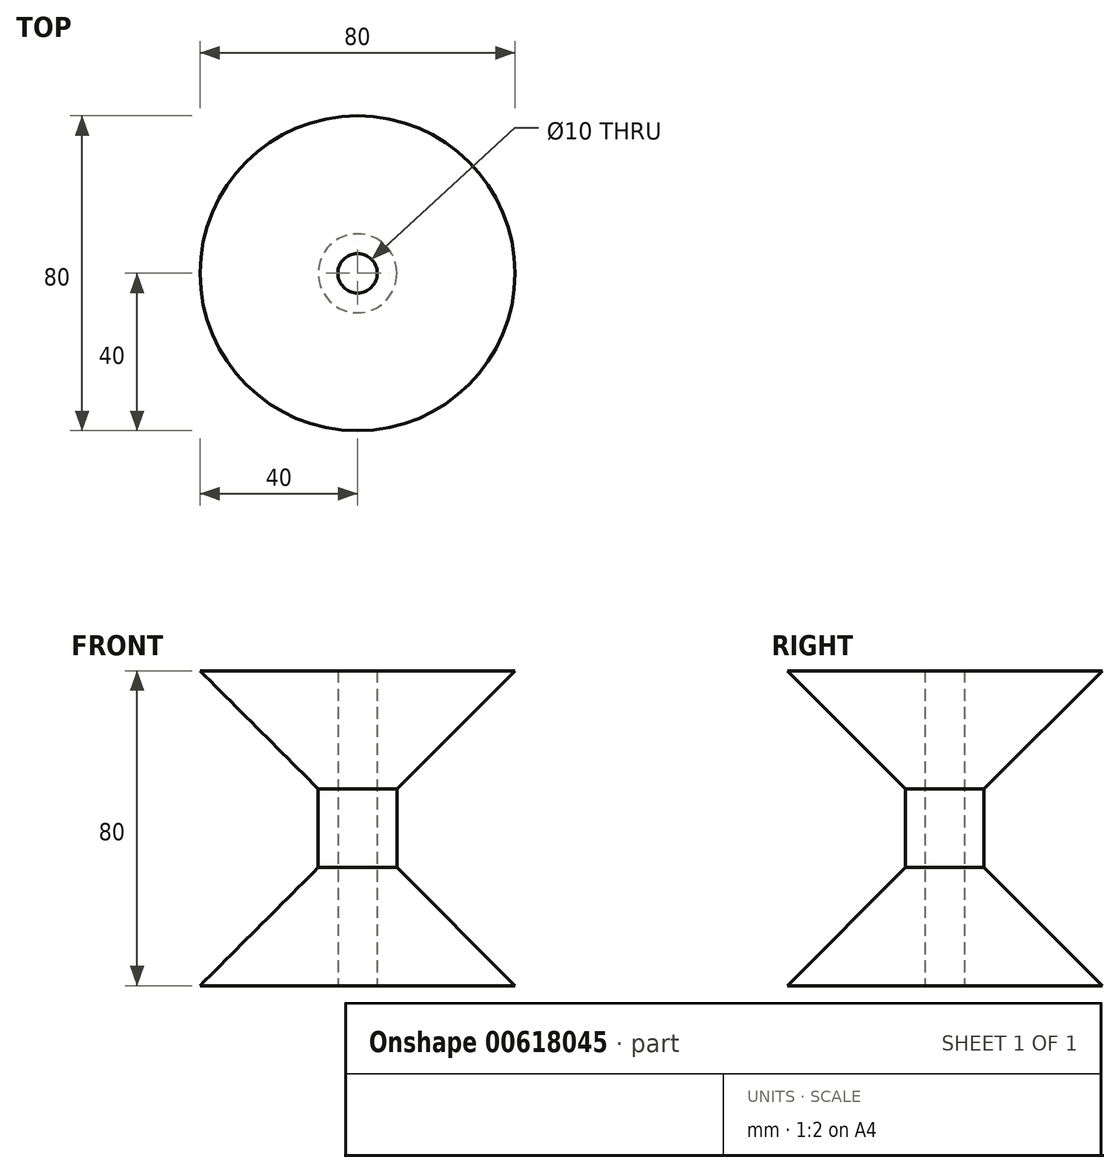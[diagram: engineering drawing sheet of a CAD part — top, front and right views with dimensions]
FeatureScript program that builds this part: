
annotation { "Feature Type Name" : "Feature", "Feature Type Description" : "" }
export const myFeature = defineFeature(function(context is Context, id is Id, definition is map)
    precondition{}
    {
        {
            var Q0;
            Q0=qCreatedBy(makeId("Front.planeOp"),FACE);
            var sketch = newSketch(context, id + "F0", { "sketchPlane" : qUnion([Q0])});
            skLineSegment(sketch, "E0", {"start": v(0, 80) * mm, "end": v(-40, 80) * mm});
            skLineSegment(sketch, "E1", {"start": v(-40, 80) * mm, "end": v(-10, 50) * mm});
            skLineSegment(sketch, "E2", {"start": v(-10, 50) * mm, "end": v(-10, 30) * mm});
            skLineSegment(sketch, "E3", {"start": v(-10, 30) * mm, "end": v(-40, 0) * mm});
            skLineSegment(sketch, "E4", {"start": v(-40, 0) * mm, "end": v(0, 0) * mm});
            skLineSegment(sketch, "E5", {"start": v(0, 0) * mm, "end": v(0, 80) * mm});
            skSolve(sketch);
        }
        {
            var Q0;
            Q0 = qSketchRegion(id + "F0", true);
            var Q1;
            Q1=sQuery(id+"F0.wireOp",EDGE,"E5");
            revolve(context, id + "F1", {"entities" : qUnion([Q0]), "axis" : qUnion([Q1]), "revolveType" : RevolveType.FULL});
        }
        {
            var Q0;
            Q0=makeQuery(id+"F1.opRevolve","SWEPT_FACE",FACE,{"disambiguationData":[OSD([sQuery(id+"F0.wireOp",EDGE,"E4")])]});
            var sketch = newSketch(context, id + "F2", { "sketchPlane" : qUnion([Q0])});
            skCircle(sketch, "E6", {"center": v(0, 0) * mm, "radius": 5 * mm});
            skSolve(sketch);
        }
        {
            var Q0;
            Q0=makeQuery(id+"F2.imprint","IMPRINT",FACE,{"disambiguationData":[TD([[makeQuery(id+"F2.imprint","IMPRINT",EDGE,{"derivedFrom":sQuery(id+"F2.wireOp",EDGE,"E6")}),1.0]])]});
            extrude(context, id + "F3", {"entities" : qUnion([Q0]), "operationType" : NewBodyOperationType.REMOVE, "endBound" : BoundingType.UP_TO_NEXT, "oppositeDirection" : true, "depth" : 25 * mm, "offsetDistance" : 25 * mm});
        }
    });
